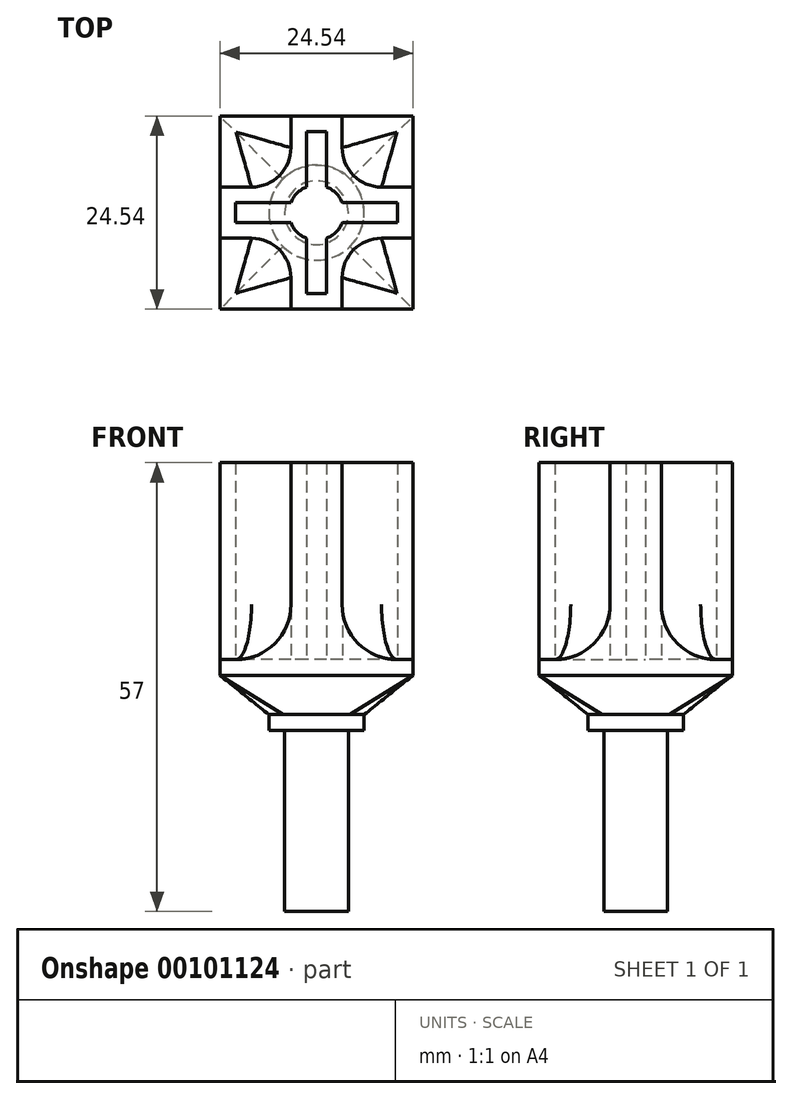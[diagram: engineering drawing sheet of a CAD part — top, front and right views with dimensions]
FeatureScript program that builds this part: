
annotation { "Feature Type Name" : "Feature", "Feature Type Description" : "" }
export const myFeature = defineFeature(function(context is Context, id is Id, definition is map)
    precondition{}
    {
        {
            var Q0;
            Q0=qCreatedBy(makeId("Top.planeOp"),FACE);
            var sketch = newSketch(context, id + "F0", { "sketchPlane" : qUnion([Q0])});
            skCircle(sketch, "E0", {"center": v(0, 0) * mm, "radius": 3.5 * mm});
            skLineSegment(sketch, "E1", {"start": v(-3.27, 1.25) * mm, "end": v(-10.27, 1.25) * mm});
            skLineSegment(sketch, "E2", {"start": v(-10.27, 1.25) * mm, "end": v(-10.27, -1.25) * mm});
            skLineSegment(sketch, "E3", {"start": v(-10.27, -1.25) * mm, "end": v(-3.27, -1.25) * mm});
            skCircle(sketch, "E4", {"center": v(0, 0) * mm, "radius": 4.5 * mm});
            skLineSegment(sketch, "E5", {"start": v(-1.3, -3.25) * mm, "end": v(-12.27, -3.25) * mm});
            skLineSegment(sketch, "E6", {"start": v(-12.27, -3.25) * mm, "end": v(-12.27, 3.25) * mm});
            skLineSegment(sketch, "E7", {"start": v(-12.27, 3.25) * mm, "end": v(-1.3, 3.25) * mm});
            skLineSegment(sketch, "E8.1.0", {"start": v(-3.25, -12.27) * mm, "end": v(-3.25, -1.3) * mm});
            skLineSegment(sketch, "E8.1.1", {"start": v(-1.25, -3.27) * mm, "end": v(-1.25, -10.27) * mm});
            skLineSegment(sketch, "E8.1.2", {"start": v(-1.25, -10.27) * mm, "end": v(1.25, -10.27) * mm});
            skLineSegment(sketch, "E8.1.3", {"start": v(1.25, -10.27) * mm, "end": v(1.25, -3.27) * mm});
            skLineSegment(sketch, "E8.1.4", {"start": v(3.25, -1.3) * mm, "end": v(3.25, -12.27) * mm});
            skLineSegment(sketch, "E8.1.5", {"start": v(3.25, -12.27) * mm, "end": v(-3.25, -12.27) * mm});
            skLineSegment(sketch, "E8.2.0", {"start": v(12.27, -3.25) * mm, "end": v(1.3, -3.25) * mm});
            skLineSegment(sketch, "E8.2.1", {"start": v(3.27, -1.25) * mm, "end": v(10.27, -1.25) * mm});
            skLineSegment(sketch, "E8.2.2", {"start": v(10.27, -1.25) * mm, "end": v(10.27, 1.25) * mm});
            skLineSegment(sketch, "E8.2.3", {"start": v(10.27, 1.25) * mm, "end": v(3.27, 1.25) * mm});
            skLineSegment(sketch, "E8.2.4", {"start": v(1.3, 3.25) * mm, "end": v(12.27, 3.25) * mm});
            skLineSegment(sketch, "E8.2.5", {"start": v(12.27, 3.25) * mm, "end": v(12.27, -3.25) * mm});
            skLineSegment(sketch, "E8.3.0", {"start": v(3.25, 12.27) * mm, "end": v(3.25, 1.3) * mm});
            skLineSegment(sketch, "E8.3.1", {"start": v(1.25, 3.27) * mm, "end": v(1.25, 10.27) * mm});
            skLineSegment(sketch, "E8.3.2", {"start": v(1.25, 10.27) * mm, "end": v(-1.25, 10.27) * mm});
            skLineSegment(sketch, "E8.3.3", {"start": v(-1.25, 10.27) * mm, "end": v(-1.25, 3.27) * mm});
            skLineSegment(sketch, "E8.3.4", {"start": v(-3.25, 1.3) * mm, "end": v(-3.25, 12.27) * mm});
            skLineSegment(sketch, "E8.3.5", {"start": v(-3.25, 12.27) * mm, "end": v(3.25, 12.27) * mm});
            skSolve(sketch);
        }
        {
            var Q0;
            Q0 = qSketchRegion(id + "F0", true);
            var Q1;
            {var subQ0=sQuery(id+"F0.wireOp",EDGE,"E5");var subQ1=sQuery(id+"F0.wireOp",EDGE,"E0");var subQ2=makeQuery(id+"F0.imprint","INTERSECT",VERTEX,{"derivedFrom":[subQ1,subQ0]});Q1=makeQuery(id+"F0.imprint","IMPRINT",FACE,{"disambiguationData":[TD([[makeQuery(id+"F0.imprint","IMPRINT",EDGE,{"disambiguationData":[TD([[subQ2,1.0]])],"derivedFrom":subQ1}),-1.0]])]});}
            var Q2;
            {var subQ0=sQuery(id+"F0.wireOp",EDGE,"E3");var subQ1=sQuery(id+"F0.wireOp",EDGE,"E0");var subQ2=makeQuery(id+"F0.imprint","INTERSECT",VERTEX,{"derivedFrom":[subQ1,subQ0]});Q2=makeQuery(id+"F0.imprint","IMPRINT",FACE,{"disambiguationData":[TD([[makeQuery(id+"F0.imprint","IMPRINT",EDGE,{"disambiguationData":[TD([[subQ2,-1.0]])],"derivedFrom":subQ1}),-1.0]])]});}
            var Q3;
            {var subQ0=sQuery(id+"F0.wireOp",EDGE,"E5");var subQ1=sQuery(id+"F0.wireOp",EDGE,"E0");var subQ2=makeQuery(id+"F0.imprint","INTERSECT",VERTEX,{"derivedFrom":[subQ1,subQ0]});Q3=makeQuery(id+"F0.imprint","IMPRINT",FACE,{"disambiguationData":[TD([[makeQuery(id+"F0.imprint","IMPRINT",EDGE,{"disambiguationData":[TD([[subQ2,-1.0]])],"derivedFrom":subQ1}),-1.0]])]});}
            var Q4;
            {var subQ0=sQuery(id+"F0.wireOp",EDGE,"E1");var subQ1=sQuery(id+"F0.wireOp",EDGE,"E0");var subQ2=makeQuery(id+"F0.imprint","INTERSECT",VERTEX,{"derivedFrom":[subQ1,subQ0]});Q4=makeQuery(id+"F0.imprint","IMPRINT",FACE,{"disambiguationData":[TD([[makeQuery(id+"F0.imprint","IMPRINT",EDGE,{"disambiguationData":[TD([[subQ2,1.0]])],"derivedFrom":subQ1}),-1.0]])]});}
            var Q5;
            {var subQ0=sQuery(id+"F0.wireOp",EDGE,"E7");var subQ1=sQuery(id+"F0.wireOp",EDGE,"E0");var subQ2=makeQuery(id+"F0.imprint","INTERSECT",VERTEX,{"derivedFrom":[subQ1,subQ0]});Q5=makeQuery(id+"F0.imprint","IMPRINT",FACE,{"disambiguationData":[TD([[makeQuery(id+"F0.imprint","IMPRINT",EDGE,{"disambiguationData":[TD([[subQ2,-1.0]])],"derivedFrom":subQ1}),-1.0]])]});}
            var Q6;
            {var subQ0=sQuery(id+"F0.wireOp",EDGE,"E7");var subQ1=sQuery(id+"F0.wireOp",EDGE,"E0");var subQ2=makeQuery(id+"F0.imprint","INTERSECT",VERTEX,{"derivedFrom":[subQ1,subQ0]});Q6=makeQuery(id+"F0.imprint","IMPRINT",FACE,{"disambiguationData":[TD([[makeQuery(id+"F0.imprint","IMPRINT",EDGE,{"disambiguationData":[TD([[subQ2,1.0]])],"derivedFrom":subQ1}),-1.0]])]});}
            var Q7;
            {var subQ0=sQuery(id+"F0.wireOp",EDGE,"E8.2.4");var subQ1=sQuery(id+"F0.wireOp",EDGE,"E0");var subQ2=makeQuery(id+"F0.imprint","INTERSECT",VERTEX,{"derivedFrom":[subQ1,subQ0]});Q7=makeQuery(id+"F0.imprint","IMPRINT",FACE,{"disambiguationData":[TD([[makeQuery(id+"F0.imprint","IMPRINT",EDGE,{"disambiguationData":[TD([[subQ2,-1.0]])],"derivedFrom":subQ1}),-1.0]])]});}
            var Q8;
            {var subQ0=sQuery(id+"F0.wireOp",EDGE,"E8.2.4");var subQ1=sQuery(id+"F0.wireOp",EDGE,"E0");var subQ2=makeQuery(id+"F0.imprint","INTERSECT",VERTEX,{"derivedFrom":[subQ1,subQ0]});Q8=makeQuery(id+"F0.imprint","IMPRINT",FACE,{"disambiguationData":[TD([[makeQuery(id+"F0.imprint","IMPRINT",EDGE,{"disambiguationData":[TD([[subQ2,1.0]])],"derivedFrom":subQ1}),-1.0]])]});}
            var Q9;
            {var subQ0=sQuery(id+"F0.wireOp",EDGE,"E8.2.3");var subQ1=sQuery(id+"F0.wireOp",EDGE,"E0");var subQ2=makeQuery(id+"F0.imprint","INTERSECT",VERTEX,{"derivedFrom":[subQ1,subQ0]});Q9=makeQuery(id+"F0.imprint","IMPRINT",FACE,{"disambiguationData":[TD([[makeQuery(id+"F0.imprint","IMPRINT",EDGE,{"disambiguationData":[TD([[subQ2,-1.0]])],"derivedFrom":subQ1}),-1.0]])]});}
            var Q10;
            {var subQ0=sQuery(id+"F0.wireOp",EDGE,"E8.1.4");var subQ1=sQuery(id+"F0.wireOp",EDGE,"E0");var subQ2=makeQuery(id+"F0.imprint","INTERSECT",VERTEX,{"derivedFrom":[subQ1,subQ0]});Q10=makeQuery(id+"F0.imprint","IMPRINT",FACE,{"disambiguationData":[TD([[makeQuery(id+"F0.imprint","IMPRINT",EDGE,{"disambiguationData":[TD([[subQ2,1.0]])],"derivedFrom":subQ1}),-1.0]])]});}
            var Q11;
            {var subQ0=sQuery(id+"F0.wireOp",EDGE,"E8.1.3");var subQ1=sQuery(id+"F0.wireOp",EDGE,"E0");var subQ2=makeQuery(id+"F0.imprint","INTERSECT",VERTEX,{"derivedFrom":[subQ1,subQ0]});Q11=makeQuery(id+"F0.imprint","IMPRINT",FACE,{"disambiguationData":[TD([[makeQuery(id+"F0.imprint","IMPRINT",EDGE,{"disambiguationData":[TD([[subQ2,-1.0]])],"derivedFrom":subQ1}),-1.0]])]});}
            var Q12;
            {var subQ0=sQuery(id+"F0.wireOp",EDGE,"E8.1.4");var subQ1=sQuery(id+"F0.wireOp",EDGE,"E0");var subQ2=makeQuery(id+"F0.imprint","INTERSECT",VERTEX,{"derivedFrom":[subQ1,subQ0]});Q12=makeQuery(id+"F0.imprint","IMPRINT",FACE,{"disambiguationData":[TD([[makeQuery(id+"F0.imprint","IMPRINT",EDGE,{"disambiguationData":[TD([[subQ2,-1.0]])],"derivedFrom":subQ1}),-1.0]])]});}
            extrude(context, id + "F1", {"entities" : qUnion([Q0, Q1, Q2, Q3, Q4, Q5, Q6, Q7, Q8, Q9, Q10, Q11, Q12]), "depth" : 25 * mm});
        }
        {
            var Q0;
            Q0=makeQuery(id+"F1.opExtrude","CAP_FACE",FACE,{"disambiguationData":[OSD([sQuery(id+"F0.wireOp",EDGE,"E0"),sQuery(id+"F0.wireOp",EDGE,"E1"),sQuery(id+"F0.wireOp",EDGE,"E2"),sQuery(id+"F0.wireOp",EDGE,"E3"),sQuery(id+"F0.wireOp",EDGE,"E5"),sQuery(id+"F0.wireOp",EDGE,"E6"),sQuery(id+"F0.wireOp",EDGE,"E7"),sQuery(id+"F0.wireOp",EDGE,"E8.1.0"),sQuery(id+"F0.wireOp",EDGE,"E8.1.1"),sQuery(id+"F0.wireOp",EDGE,"E8.1.2"),sQuery(id+"F0.wireOp",EDGE,"E8.1.3"),sQuery(id+"F0.wireOp",EDGE,"E8.1.4"),sQuery(id+"F0.wireOp",EDGE,"E8.1.5"),sQuery(id+"F0.wireOp",EDGE,"E8.2.0"),sQuery(id+"F0.wireOp",EDGE,"E8.2.1"),sQuery(id+"F0.wireOp",EDGE,"E8.2.2"),sQuery(id+"F0.wireOp",EDGE,"E8.2.3"),sQuery(id+"F0.wireOp",EDGE,"E8.2.4"),sQuery(id+"F0.wireOp",EDGE,"E8.2.5"),sQuery(id+"F0.wireOp",EDGE,"E8.3.0"),sQuery(id+"F0.wireOp",EDGE,"E8.3.1"),sQuery(id+"F0.wireOp",EDGE,"E8.3.2"),sQuery(id+"F0.wireOp",EDGE,"E8.3.3"),sQuery(id+"F0.wireOp",EDGE,"E8.3.4"),sQuery(id+"F0.wireOp",EDGE,"E8.3.5")])],"isStart":true});
            var sketch = newSketch(context, id + "F2", { "sketchPlane" : qUnion([Q0])});
            skLineSegment(sketch, "E9.bottom", {"start": v(-12.27, 12.27) * mm, "end": v(12.27, 12.27) * mm});
            skLineSegment(sketch, "E9.top", {"start": v(-12.27, -12.27) * mm, "end": v(12.27, -12.27) * mm});
            skLineSegment(sketch, "E9.left", {"start": v(-12.27, 12.27) * mm, "end": v(-12.27, -12.27) * mm});
            skLineSegment(sketch, "E9.right", {"start": v(12.27, 12.27) * mm, "end": v(12.27, -12.27) * mm});
            skSolve(sketch);
        }
        {
            var Q0;
            Q0 = qSketchRegion(id + "F2", true);
            extrude(context, id + "F3", {"entities" : qUnion([Q0]), "operationType" : NewBodyOperationType.ADD, "depth" : 2 * mm});
        }
        {
            var Q0;
            Q0=makeQuery(id+"F3.opExtrude","CAP_FACE",FACE,{"disambiguationData":[OSD([sQuery(id+"F2.wireOp",EDGE,"E9.bottom"),sQuery(id+"F2.wireOp",EDGE,"E9.top"),sQuery(id+"F2.wireOp",EDGE,"E9.left"),sQuery(id+"F2.wireOp",EDGE,"E9.right")])],"isStart":false});
            cPlane(context, id + "F4", {"entities" : qUnion([Q0]), "cplaneType" : CPlaneType.OFFSET, "offset" : 5 * mm, "width" : 150 * mm, "height" : 150 * mm});
        }
        {
            var Q0;
            Q0=qCreatedBy(id+"F4.planeOp",FACE);
            var sketch = newSketch(context, id + "F5", { "sketchPlane" : qUnion([Q0])});
            skCircle(sketch, "E10", {"center": v(0, 0) * mm, "radius": 4.05 * mm});
            skCircle(sketch, "E11", {"center": v(0, 0) * mm, "radius": 6.05 * mm});
            skSolve(sketch);
        }
        {
            var Q0;
            Q0=makeQuery(id+"F5.imprint","IMPRINT",FACE,{"disambiguationData":[TD([[makeQuery(id+"F5.imprint","IMPRINT",EDGE,{"derivedFrom":sQuery(id+"F5.wireOp",EDGE,"E10")}),1.0]])]});
            extrude(context, id + "F6", {"entities" : qUnion([Q0]), "depth" : 25 * mm});
        }
        {
            var Q0;
            Q0=makeQuery(id+"F5.imprint","IMPRINT",FACE,{"disambiguationData":[TD([[makeQuery(id+"F5.imprint","IMPRINT",EDGE,{"derivedFrom":sQuery(id+"F5.wireOp",EDGE,"E10")}),-1.0]])]});
            extrude(context, id + "F7", {"entities" : qUnion([Q0]), "operationType" : NewBodyOperationType.ADD, "depth" : 2 * mm});
        }
        {
            var Q1;
            {var subQ0=sQuery(id+"F5.wireOp",EDGE,"E10");Q1=makeQuery(id+"F7.boolean.opBoolean","MERGE",FACE,{"derivedFrom":[makeQuery(id+"F6.opExtrude","CAP_FACE",FACE,{"disambiguationData":[OSD([subQ0])],"isStart":true}),makeQuery(id+"F7.opExtrude","CAP_FACE",FACE,{"disambiguationData":[OSD([subQ0,sQuery(id+"F5.wireOp",EDGE,"E11")])],"isStart":true})]});}
            var Q2;
            Q2=makeQuery(id+"F3.opExtrude","CAP_FACE",FACE,{"disambiguationData":[OSD([sQuery(id+"F2.wireOp",EDGE,"E9.bottom"),sQuery(id+"F2.wireOp",EDGE,"E9.top"),sQuery(id+"F2.wireOp",EDGE,"E9.left"),sQuery(id+"F2.wireOp",EDGE,"E9.right")])],"isStart":false});
            loft(context, id + "F8", {"operationType" : NewBodyOperationType.ADD, "sheetProfilesArray" : [{ "sheetProfileEntities" : qUnion([Q1]) }, { "sheetProfileEntities" : qUnion([Q2]) }]});
        }
        {
            var Q0;
            Q0=makeQuery(id+"F1.opExtrude","CAP_EDGE",EDGE,{"disambiguationData":[OSD([sQuery(id+"F0.wireOp",EDGE,"E7")])],"isStart":true});
            var Q1;
            Q1=makeQuery(id+"F1.opExtrude","CAP_EDGE",EDGE,{"disambiguationData":[OSD([sQuery(id+"F0.wireOp",EDGE,"E8.3.4")])],"isStart":true});
            var Q2;
            Q2=makeQuery(id+"F1.opExtrude","CAP_EDGE",EDGE,{"disambiguationData":[OSD([sQuery(id+"F0.wireOp",EDGE,"E8.3.0")])],"isStart":true});
            var Q3;
            Q3=makeQuery(id+"F1.opExtrude","CAP_EDGE",EDGE,{"disambiguationData":[OSD([sQuery(id+"F0.wireOp",EDGE,"E8.2.4")])],"isStart":true});
            var Q4;
            Q4=makeQuery(id+"F1.opExtrude","CAP_EDGE",EDGE,{"disambiguationData":[OSD([sQuery(id+"F0.wireOp",EDGE,"E5")])],"isStart":true});
            var Q5;
            Q5=makeQuery(id+"F1.opExtrude","CAP_EDGE",EDGE,{"disambiguationData":[OSD([sQuery(id+"F0.wireOp",EDGE,"E8.1.0")])],"isStart":true});
            var Q6;
            Q6=makeQuery(id+"F1.opExtrude","CAP_EDGE",EDGE,{"disambiguationData":[OSD([sQuery(id+"F0.wireOp",EDGE,"E8.1.4")])],"isStart":true});
            var Q7;
            Q7=makeQuery(id+"F1.opExtrude","CAP_EDGE",EDGE,{"disambiguationData":[OSD([sQuery(id+"F0.wireOp",EDGE,"E8.2.0")])],"isStart":true});
            fillet(context, id + "F9", {"entities" : qUnion([Q0, Q1, Q2, Q3, Q4, Q5, Q6, Q7]), "radius" : 7 * mm, "tangentPropagation" : true, "allowEdgeOverflow" : false});
        }
        {
            var Q0;
            Q0=makeQuery(id+"F9.opFillet","BLEND_EDGE",EDGE,{"blendedFrom":[makeQuery(id+"F1.opExtrude","CAP_EDGE",EDGE,{"disambiguationData":[OSD([sQuery(id+"F0.wireOp",EDGE,"E5")])],"isStart":true}),makeQuery(id+"F1.opExtrude","CAP_EDGE",EDGE,{"disambiguationData":[OSD([sQuery(id+"F0.wireOp",EDGE,"E8.1.0")])],"isStart":true})],"blendedInto":[]});
            var Q1;
            Q1=makeQuery(id+"F9.opFillet","BLEND_EDGE",EDGE,{"blendedFrom":[makeQuery(id+"F1.opExtrude","CAP_EDGE",EDGE,{"disambiguationData":[OSD([sQuery(id+"F0.wireOp",EDGE,"E7")])],"isStart":true}),makeQuery(id+"F1.opExtrude","CAP_EDGE",EDGE,{"disambiguationData":[OSD([sQuery(id+"F0.wireOp",EDGE,"E8.3.4")])],"isStart":true})],"blendedInto":[]});
            var Q2;
            Q2=makeQuery(id+"F9.opFillet","BLEND_EDGE",EDGE,{"blendedFrom":[makeQuery(id+"F1.opExtrude","CAP_EDGE",EDGE,{"disambiguationData":[OSD([sQuery(id+"F0.wireOp",EDGE,"E8.2.4")])],"isStart":true}),makeQuery(id+"F1.opExtrude","CAP_EDGE",EDGE,{"disambiguationData":[OSD([sQuery(id+"F0.wireOp",EDGE,"E8.3.0")])],"isStart":true})],"blendedInto":[]});
            var Q3;
            Q3=makeQuery(id+"F9.opFillet","BLEND_EDGE",EDGE,{"blendedFrom":[makeQuery(id+"F1.opExtrude","CAP_EDGE",EDGE,{"disambiguationData":[OSD([sQuery(id+"F0.wireOp",EDGE,"E8.1.4")])],"isStart":true}),makeQuery(id+"F1.opExtrude","CAP_EDGE",EDGE,{"disambiguationData":[OSD([sQuery(id+"F0.wireOp",EDGE,"E8.2.0")])],"isStart":true})],"blendedInto":[]});
            fillet(context, id + "F10", {"entities" : qUnion([Q0, Q1, Q2, Q3]), "radius" : 5 * mm, "tangentPropagation" : true, "allowEdgeOverflow" : false});
        }
    });
